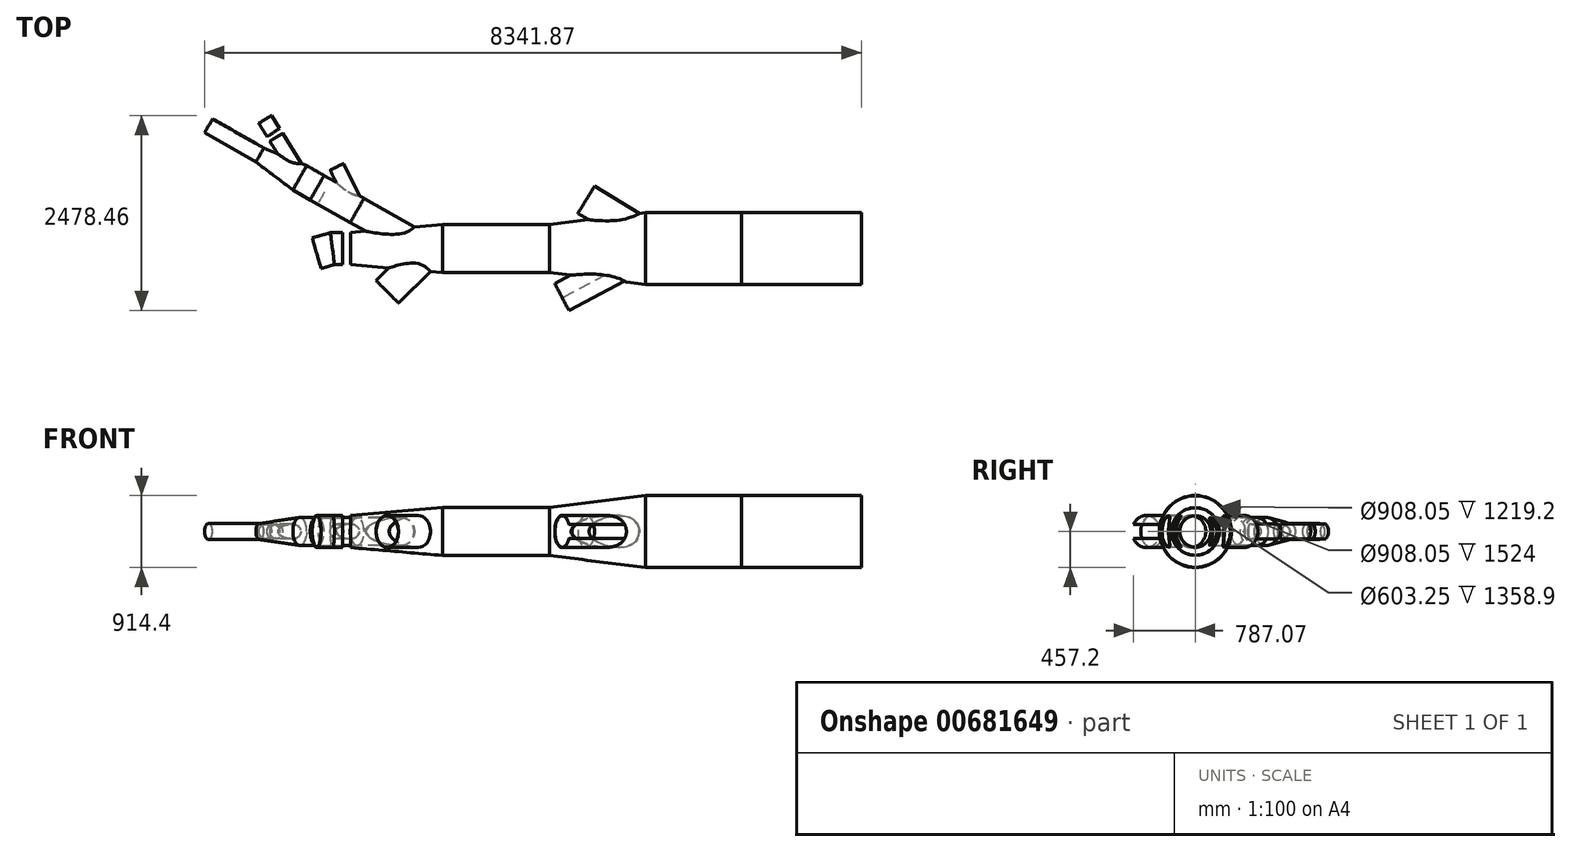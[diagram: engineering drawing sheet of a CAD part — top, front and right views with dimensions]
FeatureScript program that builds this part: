
annotation { "Feature Type Name" : "Feature", "Feature Type Description" : "" }
export const myFeature = defineFeature(function(context is Context, id is Id, definition is map)
    precondition{}
    {
        {
            var Q0;
            Q0=qCreatedBy(makeId("Top.planeOp"),FACE);
            var sketch = newSketch(context, id + "F0", { "sketchPlane" : qUnion([Q0])});
            skLineSegment(sketch, "E0", {"start": v(0, 0) * mm, "end": v(1524, 0) * mm, "construction": true});
            skLineSegment(sketch, "E1", {"start": v(0, 0) * mm, "end": v(-1219.2, 0) * mm, "construction": true});
            skLineSegment(sketch, "E2", {"start": v(-1219.2, 0) * mm, "end": v(-2438.4, 0) * mm, "construction": true});
            skLineSegment(sketch, "E3", {"start": v(-2438.4, 0) * mm, "end": v(-3797.3, 0) * mm, "construction": true});
            skLineSegment(sketch, "E4", {"start": v(-3797.3, 0) * mm, "end": v(-4965.7, 0) * mm, "construction": true});
            skLineSegment(sketch, "E5", {"start": v(-4965.7, 0) * mm, "end": v(-5067.3, 0) * mm, "construction": true});
            skLineSegment(sketch, "E6", {"start": v(1524, 0) * mm, "end": v(1524, 457.2) * mm, "construction": true});
            skLineSegment(sketch, "E7", {"start": v(1524, 0) * mm, "end": v(1524, -457.2) * mm, "construction": true});
            skLineSegment(sketch, "E8", {"start": v(0, 0) * mm, "end": v(0, 457.2) * mm, "construction": true});
            skLineSegment(sketch, "E9", {"start": v(0, 0) * mm, "end": v(0, -457.2) * mm, "construction": true});
            skLineSegment(sketch, "E10", {"start": v(-1219.2, 0) * mm, "end": v(-1219.2, 457.2) * mm, "construction": true});
            skLineSegment(sketch, "E11", {"start": v(-1219.2, 0) * mm, "end": v(-1219.2, -457.2) * mm, "construction": true});
            skLineSegment(sketch, "E12", {"start": v(-2438.4, 0) * mm, "end": v(-2438.4, 304.8) * mm, "construction": true});
            skLineSegment(sketch, "E13", {"start": v(-2438.4, 0) * mm, "end": v(-2438.4, -304.8) * mm, "construction": true});
            skLineSegment(sketch, "E14", {"start": v(-3797.3, 0) * mm, "end": v(-3797.3, 304.8) * mm, "construction": true});
            skLineSegment(sketch, "E15", {"start": v(-3797.3, 0) * mm, "end": v(-3797.3, -304.8) * mm, "construction": true});
            skLineSegment(sketch, "E16", {"start": v(-4965.7, 0) * mm, "end": v(-4965.7, 203.2) * mm, "construction": true});
            skLineSegment(sketch, "E17", {"start": v(-4965.7, 0) * mm, "end": v(-4965.7, -203.2) * mm, "construction": true});
            skLineSegment(sketch, "E18", {"start": v(-5067.3, 0) * mm, "end": v(-5067.3, 203.2) * mm, "construction": true});
            skLineSegment(sketch, "E19", {"start": v(-5067.3, 0) * mm, "end": v(-5067.3, -203.2) * mm, "construction": true});
            skLineSegment(sketch, "E20", {"start": v(-5067.3, 203.2) * mm, "end": v(-5219.7, 203.2) * mm, "construction": true});
            skLineSegment(sketch, "E21", {"start": v(-5067.3, -203.2) * mm, "end": v(-5168.9, -203.2) * mm, "construction": true});
            skLineSegment(sketch, "E22", {"start": v(-5168.9, -203.2) * mm, "end": v(-5219.7, 203.2) * mm, "construction": true});
            skLineSegment(sketch, "E23", {"start": v(-5219.7, 203.2) * mm, "end": v(-5451.6, 136.5) * mm, "construction": true});
            skLineSegment(sketch, "E24", {"start": v(-5451.6, 136.5) * mm, "end": v(-5339.27, -254.06) * mm, "construction": true});
            skLineSegment(sketch, "E25", {"start": v(-5339.27, -254.06) * mm, "end": v(-5168.9, -203.2) * mm, "construction": true});
            skLineSegment(sketch, "E26", {"start": v(-4965.7, -203.2) * mm, "end": v(-3797.3, -304.8) * mm, "construction": true});
            skLineSegment(sketch, "E27", {"start": v(-1219.2, 457.2) * mm, "end": v(0, 457.2) * mm, "construction": true});
            skLineSegment(sketch, "E28", {"start": v(1524, 457.2) * mm, "end": v(0, 457.2) * mm, "construction": true});
            skLineSegment(sketch, "E29", {"start": v(-1219.2, -457.2) * mm, "end": v(0, -457.2) * mm, "construction": true});
            skLineSegment(sketch, "E30", {"start": v(1524, -457.2) * mm, "end": v(0, -457.2) * mm, "construction": true});
            skLineSegment(sketch, "E31", {"start": v(-3797.3, 304.8) * mm, "end": v(-2438.4, 304.8) * mm, "construction": true});
            skLineSegment(sketch, "E32", {"start": v(-3797.3, -304.8) * mm, "end": v(-2438.4, -304.8) * mm, "construction": true});
            skLineSegment(sketch, "E33", {"start": v(-5067.3, 203.2) * mm, "end": v(-4965.7, 203.2) * mm, "construction": true});
            skLineSegment(sketch, "E34", {"start": v(-5067.3, -203.2) * mm, "end": v(-4965.7, -203.2) * mm, "construction": true});
            skLineSegment(sketch, "E35", {"start": v(-2438.4, 304.8) * mm, "end": v(-1946.92, 366.23) * mm, "construction": true});
            skLineSegment(sketch, "E36", {"start": v(-1946.92, 366.23) * mm, "end": v(-2077.03, 445.6) * mm});
            skLineSegment(sketch, "E37", {"start": v(-2077.03, 445.6) * mm, "end": v(-1865.38, 792.54) * mm});
            skLineSegment(sketch, "E38", {"start": v(-1865.38, 792.54) * mm, "end": v(-1301.6, 448.62) * mm});
            skLineSegment(sketch, "E39", {"start": v(-2438.4, -304.8) * mm, "end": v(-2167.46, -338.67) * mm, "construction": true});
            skLineSegment(sketch, "E40", {"start": v(-2167.46, -338.67) * mm, "end": v(-2369.86, -444.93) * mm});
            skLineSegment(sketch, "E41", {"start": v(-2369.86, -444.93) * mm, "end": v(-2180.95, -804.75) * mm});
            skLineSegment(sketch, "E42", {"start": v(-2180.95, -804.75) * mm, "end": v(-1461.3, -426.94) * mm});
            skLineSegment(sketch, "E43", {"start": v(-2167.46, -338.67) * mm, "end": v(-1219.2, -457.2) * mm, "construction": true});
            skLineSegment(sketch, "E44", {"start": v(-1946.92, 366.23) * mm, "end": v(-1219.2, 457.2) * mm, "construction": true});
            skLineSegment(sketch, "E45", {"start": v(-4965.7, 203.2) * mm, "end": v(-4775.92, 219.7) * mm, "construction": true});
            skLineSegment(sketch, "E46", {"start": v(-4775.92, 219.7) * mm, "end": v(-4969, 329.78) * mm});
            skLineSegment(sketch, "E47", {"start": v(-4969, 329.78) * mm, "end": v(-4792.87, 638.7) * mm, "construction": true});
            skLineSegment(sketch, "E48", {"start": v(-4792.87, 638.7) * mm, "end": v(-4152.96, 273.87) * mm});
            skLineSegment(sketch, "E49", {"start": v(-4775.92, 219.7) * mm, "end": v(-3797.3, 304.8) * mm, "construction": true});
            skLineSegment(sketch, "E50", {"start": v(-4965.7, -203.2) * mm, "end": v(-4478.59, -245.56) * mm, "construction": true});
            skLineSegment(sketch, "E51", {"start": v(-4478.59, -245.56) * mm, "end": v(-4640.5, -406.93) * mm});
            skLineSegment(sketch, "E52", {"start": v(-4640.5, -406.93) * mm, "end": v(-4353.62, -694.78) * mm});
            skLineSegment(sketch, "E53", {"start": v(-4353.62, -694.78) * mm, "end": v(-3948.83, -291.35) * mm});
            skLineSegment(sketch, "E54", {"start": v(-1971.2, 619.07) * mm, "end": v(-1623.1, 406.71) * mm, "construction": true});
            skLineSegment(sketch, "E55", {"start": v(-4497.06, -550.86) * mm, "end": v(-4213.84, -268.58) * mm, "construction": true});
            skLineSegment(sketch, "E56", {"start": v(-4880.93, 484.24) * mm, "end": v(-4464.44, 246.79) * mm, "construction": true});
            skLineSegment(sketch, "E57", {"start": v(-2275.4, -624.84) * mm, "end": v(-1814.38, -382.8) * mm, "construction": true});
            skLineSegment(sketch, "E58", {"start": v(-5395.43, -58.78) * mm, "end": v(-5194.19, -0.9) * mm, "construction": true});
            skLineSegment(sketch, "E59", {"start": v(-5067.3, 0) * mm, "end": v(-5194.19, -0.9) * mm, "construction": true});
            skLineSegment(sketch, "E60", {"start": v(-4880.93, 484.24) * mm, "end": v(-5388.44, 773.59) * mm, "construction": true});
            skLineSegment(sketch, "E61", {"start": v(-5388.44, 773.59) * mm, "end": v(-5609.1, 899.39) * mm, "construction": true});
            skLineSegment(sketch, "E62", {"start": v(-5609.1, 899.39) * mm, "end": v(-6116.61, 1188.74) * mm, "construction": true});
            skLineSegment(sketch, "E63", {"start": v(-6116.61, 1188.74) * mm, "end": v(-6767.55, 1559.85) * mm, "construction": true});
            skLineSegment(sketch, "E64", {"start": v(-6767.55, 1559.85) * mm, "end": v(-6717.23, 1648.12) * mm, "construction": true});
            skLineSegment(sketch, "E65", {"start": v(-6767.55, 1559.85) * mm, "end": v(-6817.87, 1471.6) * mm, "construction": true});
            skLineSegment(sketch, "E66", {"start": v(-5388.44, 773.59) * mm, "end": v(-5300.38, 928.05) * mm, "construction": true});
            skLineSegment(sketch, "E67", {"start": v(-5609.1, 899.39) * mm, "end": v(-5521.04, 1053.85) * mm, "construction": true});
            skLineSegment(sketch, "E68", {"start": v(-6116.61, 1188.74) * mm, "end": v(-6066.29, 1277) * mm, "construction": true});
            skLineSegment(sketch, "E69", {"start": v(-5388.44, 773.59) * mm, "end": v(-5476.5, 619.13) * mm, "construction": true});
            skLineSegment(sketch, "E70", {"start": v(-5609.1, 899.39) * mm, "end": v(-5697.16, 744.93) * mm, "construction": true});
            skLineSegment(sketch, "E71", {"start": v(-6116.61, 1188.74) * mm, "end": v(-6166.93, 1100.47) * mm, "construction": true});
            skLineSegment(sketch, "E72", {"start": v(-6066.29, 1277) * mm, "end": v(-5521.04, 1053.85) * mm, "construction": true});
            skLineSegment(sketch, "E73", {"start": v(-4792.87, 638.7) * mm, "end": v(-5300.38, 928.05) * mm, "construction": true});
            skLineSegment(sketch, "E74", {"start": v(-5300.38, 928.05) * mm, "end": v(-5156.95, 846.28) * mm});
            skLineSegment(sketch, "E75", {"start": v(-5156.95, 846.28) * mm, "end": v(-5228.95, 994.85) * mm});
            skLineSegment(sketch, "E76", {"start": v(-5228.95, 994.85) * mm, "end": v(-5046.1, 1083.46) * mm});
            skLineSegment(sketch, "E77", {"start": v(-5046.1, 1083.46) * mm, "end": v(-4846.7, 672.03) * mm});
            skLineSegment(sketch, "E78", {"start": v(-6066.29, 1277) * mm, "end": v(-5901.74, 1209.65) * mm});
            skLineSegment(sketch, "E79", {"start": v(-5901.74, 1209.65) * mm, "end": v(-5995.1, 1360.97) * mm});
            skLineSegment(sketch, "E80", {"start": v(-5995.1, 1360.97) * mm, "end": v(-5822.16, 1467.67) * mm});
            skLineSegment(sketch, "E81", {"start": v(-5822.16, 1467.67) * mm, "end": v(-5582.1, 1078.56) * mm});
            skLineSegment(sketch, "E82", {"start": v(-5908.63, 1414.32) * mm, "end": v(-5742.03, 1144.3) * mm, "construction": true});
            skLineSegment(sketch, "E83", {"start": v(-5137.52, 1039.16) * mm, "end": v(-5000.95, 757.33) * mm, "construction": true});
            skLineSegment(sketch, "E84", {"start": v(-5228.95, 994.85) * mm, "end": v(-5259.41, 1057.7) * mm});
            skLineSegment(sketch, "E85", {"start": v(-5259.41, 1057.7) * mm, "end": v(-5076.56, 1146.32) * mm, "construction": true});
            skLineSegment(sketch, "E86", {"start": v(-5076.56, 1146.32) * mm, "end": v(-5046.1, 1083.46) * mm});
            skLineSegment(sketch, "E87", {"start": v(-5995.1, 1360.97) * mm, "end": v(-6031.77, 1420.42) * mm, "construction": true});
            skLineSegment(sketch, "E88", {"start": v(-6031.77, 1420.42) * mm, "end": v(-5858.84, 1527.11) * mm, "construction": true});
            skLineSegment(sketch, "E89", {"start": v(-5858.84, 1527.11) * mm, "end": v(-5822.16, 1467.67) * mm, "construction": true});
            skLineSegment(sketch, "E90", {"start": v(-6031.77, 1420.42) * mm, "end": v(-6135.13, 1587.95) * mm, "construction": true});
            skLineSegment(sketch, "E91", {"start": v(-6135.13, 1587.95) * mm, "end": v(-6048.66, 1641.3) * mm, "construction": true});
            skLineSegment(sketch, "E92", {"start": v(-6048.66, 1641.3) * mm, "end": v(-5908.63, 1414.32) * mm, "construction": true});
            skLineSegment(sketch, "E93", {"start": v(-6048.66, 1641.3) * mm, "end": v(-5962.2, 1694.64) * mm, "construction": true});
            skLineSegment(sketch, "E94", {"start": v(-5962.2, 1694.64) * mm, "end": v(-5858.84, 1527.11) * mm, "construction": true});
            skSolve(sketch);
        }
        {
            var Q0;
            Q0=sQuery(id+"F0.wireOp",EDGE,"E7");
            cPlane(context, id + "F1", {"entities" : qUnion([Q0]), "cplaneType" : CPlaneType.LINE_ANGLE, "offset" : 0 * mm, "angle" : 90 * degree, "width" : 152.4 * mm, "height" : 152.4 * mm});
        }
        {
            var Q0;
            Q0=sQuery(id+"F0.wireOp",EDGE,"E9");
            cPlane(context, id + "F2", {"entities" : qUnion([Q0]), "cplaneType" : CPlaneType.LINE_ANGLE, "offset" : 0 * mm, "angle" : 90 * degree, "width" : 152.4 * mm, "height" : 152.4 * mm});
        }
        {
            var Q0;
            Q0=sQuery(id+"F0.wireOp",EDGE,"E11");
            cPlane(context, id + "F3", {"entities" : qUnion([Q0]), "cplaneType" : CPlaneType.LINE_ANGLE, "offset" : 0 * mm, "angle" : 90 * degree, "width" : 152.4 * mm, "height" : 152.4 * mm});
        }
        {
            var Q0;
            Q0=sQuery(id+"F0.wireOp",EDGE,"E13");
            cPlane(context, id + "F4", {"entities" : qUnion([Q0]), "cplaneType" : CPlaneType.LINE_ANGLE, "offset" : 25.4 * mm, "angle" : 90 * degree, "width" : 152.4 * mm, "height" : 152.4 * mm});
        }
        {
            var Q0;
            Q0=sQuery(id+"F0.wireOp",EDGE,"E15");
            cPlane(context, id + "F5", {"entities" : qUnion([Q0]), "cplaneType" : CPlaneType.LINE_ANGLE, "offset" : 25.4 * mm, "angle" : 90 * degree, "width" : 152.4 * mm, "height" : 152.4 * mm});
        }
        {
            var Q0;
            Q0=sQuery(id+"F0.wireOp",EDGE,"E17");
            cPlane(context, id + "F6", {"entities" : qUnion([Q0]), "cplaneType" : CPlaneType.LINE_ANGLE, "offset" : 25.4 * mm, "angle" : 90 * degree, "width" : 152.4 * mm, "height" : 152.4 * mm});
        }
        {
            var Q0;
            Q0=sQuery(id+"F0.wireOp",EDGE,"E19");
            cPlane(context, id + "F7", {"entities" : qUnion([Q0]), "cplaneType" : CPlaneType.LINE_ANGLE, "offset" : 25.4 * mm, "angle" : 90 * degree, "width" : 152.4 * mm, "height" : 152.4 * mm});
        }
        {
            var Q0;
            Q0=sQuery(id+"F0.wireOp",EDGE,"E22");
            cPlane(context, id + "F8", {"entities" : qUnion([Q0]), "cplaneType" : CPlaneType.LINE_ANGLE, "offset" : 25.4 * mm, "angle" : 90 * degree, "width" : 152.4 * mm, "height" : 152.4 * mm});
        }
        {
            var Q0;
            Q0=sQuery(id+"F0.wireOp",EDGE,"E24");
            cPlane(context, id + "F9", {"entities" : qUnion([Q0]), "cplaneType" : CPlaneType.LINE_ANGLE, "offset" : 25.4 * mm, "angle" : 90 * degree, "width" : 152.4 * mm, "height" : 152.4 * mm});
        }
        {
            var Q0;
            Q0=sQuery(id+"F0.wireOp",EDGE,"E37");
            cPlane(context, id + "F10", {"entities" : qUnion([Q0]), "cplaneType" : CPlaneType.LINE_ANGLE, "offset" : 25.4 * mm, "angle" : 90 * degree, "width" : 152.4 * mm, "height" : 152.4 * mm});
        }
        {
            var Q0;
            Q0=sQuery(id+"F0.wireOp",EDGE,"E41");
            cPlane(context, id + "F11", {"entities" : qUnion([Q0]), "cplaneType" : CPlaneType.LINE_ANGLE, "offset" : 25.4 * mm, "angle" : 90 * degree, "width" : 152.4 * mm, "height" : 152.4 * mm});
        }
        {
            var Q0;
            Q0=sQuery(id+"F0.wireOp",EDGE,"E47");
            cPlane(context, id + "F12", {"entities" : qUnion([Q0]), "cplaneType" : CPlaneType.LINE_ANGLE, "offset" : 25.4 * mm, "angle" : 90 * degree, "width" : 152.4 * mm, "height" : 152.4 * mm});
        }
        {
            var Q0;
            Q0=sQuery(id+"F0.wireOp",EDGE,"E52");
            cPlane(context, id + "F13", {"entities" : qUnion([Q0]), "cplaneType" : CPlaneType.LINE_ANGLE, "offset" : 25.4 * mm, "angle" : 90 * degree, "width" : 152.4 * mm, "height" : 152.4 * mm});
        }
        {
            var Q0;
            Q0=qCreatedBy(id+"F1.planeOp",FACE);
            var sketch = newSketch(context, id + "F14", { "sketchPlane" : qUnion([Q0])});
            skCircle(sketch, "E95", {"center": v(0, 0) * mm, "radius": 457.2 * mm});
            skCircle(sketch, "E96", {"center": v(0, 0) * mm, "radius": 454.03 * mm});
            skSolve(sketch);
        }
        {
            var Q0;
            Q0=makeQuery(id+"F14.imprint","IMPRINT",FACE,{"disambiguationData":[TD([[makeQuery(id+"F14.imprint","IMPRINT",EDGE,{"derivedFrom":sQuery(id+"F14.wireOp",EDGE,"E95")}),1.0]])]});
            extrude(context, id + "F15", {"entities" : qUnion([Q0]), "oppositeDirection" : true, "depth" : 1524 * mm, "offsetDistance" : 25.4 * mm});
        }
        {
            var Q0;
            Q0=qCreatedBy(id+"F2.planeOp",FACE);
            var sketch = newSketch(context, id + "F16", { "sketchPlane" : qUnion([Q0])});
            skCircle(sketch, "E97", {"center": v(0, 0) * mm, "radius": 454.03 * mm});
            skCircle(sketch, "E98", {"center": v(0, 0) * mm, "radius": 457.2 * mm});
            skSolve(sketch);
        }
        {
            var Q0;
            Q0=makeQuery(id+"F16.imprint","IMPRINT",FACE,{"disambiguationData":[TD([[makeQuery(id+"F16.imprint","IMPRINT",EDGE,{"derivedFrom":sQuery(id+"F16.wireOp",EDGE,"E97")}),-1.0]])]});
            extrude(context, id + "F17", {"entities" : qUnion([Q0]), "oppositeDirection" : true, "depth" : 1219.2 * mm, "offsetDistance" : 25.4 * mm});
        }
        {
            var Q0;
            Q0=qCreatedBy(id+"F3.planeOp",FACE);
            var sketch = newSketch(context, id + "F18", { "sketchPlane" : qUnion([Q0])});
            skCircle(sketch, "E99", {"center": v(0, 0) * mm, "radius": 457.2 * mm});
            skSolve(sketch);
        }
        {
            var Q0;
            Q0=qCreatedBy(id+"F4.planeOp",FACE);
            var sketch = newSketch(context, id + "F19", { "sketchPlane" : qUnion([Q0])});
            skCircle(sketch, "E100", {"center": v(0, 0) * mm, "radius": 304.8 * mm});
            skSolve(sketch);
        }
        {
            var Q0;
            Q0=qCreatedBy(id+"F10.planeOp",FACE);
            var sketch = newSketch(context, id + "F20", { "sketchPlane" : qUnion([Q0])});
            skCircle(sketch, "E101", {"center": v(-495.72, 0) * mm, "radius": 203.2 * mm});
            skSolve(sketch);
        }
        {
            var Q0;
            Q0=makeQuery(id+"F20.imprint","IMPRINT",FACE,{"disambiguationData":[TD([[makeQuery(id+"F20.imprint","IMPRINT",EDGE,{"derivedFrom":sQuery(id+"F20.wireOp",EDGE,"E101")}),1.0]])]});
            extrude(context, id + "F21", {"entities" : qUnion([Q0]), "depth" : 716.28 * mm, "offsetDistance" : 25.4 * mm});
        }
        {
            var Q0;
            Q0=qCreatedBy(id+"F11.planeOp",FACE);
            var sketch = newSketch(context, id + "F22", { "sketchPlane" : qUnion([Q0])});
            skCircle(sketch, "E102", {"center": v(504.45, 0) * mm, "radius": 203.2 * mm});
            skSolve(sketch);
        }
        {
            var Q0;
            Q0=makeQuery(id+"F22.imprint","IMPRINT",FACE,{"disambiguationData":[TD([[makeQuery(id+"F22.imprint","IMPRINT",EDGE,{"derivedFrom":sQuery(id+"F22.wireOp",EDGE,"E102")}),1.0]])]});
            extrude(context, id + "F23", {"entities" : qUnion([Q0]), "depth" : 833.12 * mm, "offsetDistance" : 25.4 * mm});
        }
        {
            var Q2;
            Q2=makeQuery(id+"F19.imprint","IMPRINT",FACE,{"disambiguationData":[TD([[makeQuery(id+"F19.imprint","IMPRINT",EDGE,{"derivedFrom":sQuery(id+"F19.wireOp",EDGE,"E100")}),1.0]])]});
            var Q3;
            Q3=makeQuery(id+"F18.imprint","IMPRINT",FACE,{"disambiguationData":[TD([[makeQuery(id+"F18.imprint","IMPRINT",EDGE,{"derivedFrom":sQuery(id+"F18.wireOp",EDGE,"E99")}),1.0]])]});
            loft(context, id + "F24", {"operationType" : NewBodyOperationType.REMOVE, "sheetProfilesArray" : [{ "sheetProfileEntities" : qUnion([Q2]) }, { "sheetProfileEntities" : qUnion([Q3]) }]});
        }
        {
            var Q0;
            Q0=qCreatedBy(id+"F4.planeOp",FACE);
            var sketch = newSketch(context, id + "F25", { "sketchPlane" : qUnion([Q0])});
            skCircle(sketch, "E103", {"center": v(0, 0) * mm, "radius": 304.8 * mm});
            skSolve(sketch);
        }
        {
            var Q0;
            Q0=qCreatedBy(id+"F3.planeOp",FACE);
            var sketch = newSketch(context, id + "F26", { "sketchPlane" : qUnion([Q0])});
            skCircle(sketch, "E104", {"center": v(0, 0) * mm, "radius": 457.2 * mm});
            skSolve(sketch);
        }
        {
            var Q0;
            Q0=makeQuery(id+"F25.imprint","IMPRINT",FACE,{"disambiguationData":[TD([[makeQuery(id+"F25.imprint","IMPRINT",EDGE,{"derivedFrom":sQuery(id+"F25.wireOp",EDGE,"E103")}),1.0]])]});
            var Q1;
            Q1=makeQuery(id+"F26.imprint","IMPRINT",FACE,{"disambiguationData":[TD([[makeQuery(id+"F26.imprint","IMPRINT",EDGE,{"derivedFrom":sQuery(id+"F26.wireOp",EDGE,"E104")}),1.0]])]});
            loft(context, id + "F27", {"sheetProfilesArray" : [{ "sheetProfileEntities" : qUnion([Q0]) }, { "sheetProfileEntities" : qUnion([Q1]) }]});
        }
        {
            var Q0;
            Q0=makeQuery(id+"F27.opLoft","CAP_FACE",FACE,{"disambiguationData":[OSD([makeQuery(id+"F26.imprint","IMPRINT",FACE,{"disambiguationData":[TD([[makeQuery(id+"F26.imprint","IMPRINT",EDGE,{"derivedFrom":sQuery(id+"F26.wireOp",EDGE,"E104")}),1.0]])]})])],"isStart":true});
            var Q1;
            Q1=makeQuery(id+"F27.opLoft","CAP_FACE",FACE,{"disambiguationData":[OSD([makeQuery(id+"F25.imprint","IMPRINT",FACE,{"disambiguationData":[TD([[makeQuery(id+"F25.imprint","IMPRINT",EDGE,{"derivedFrom":sQuery(id+"F25.wireOp",EDGE,"E103")}),1.0]])]})])],"isStart":true});
            shell(context, id + "F28", {"entities" : qUnion([Q0, Q1]), "thickness" : 2.54 * mm});
        }
        {
            var Q0;
            Q0=makeQuery(id+"F24.boolean.opBoolean","COPY",FACE,{"disambiguationData":[TD([makeQuery(id+"F23.opExtrude","SWEPT_FACE",FACE,{"disambiguationData":[OSD([sQuery(id+"F22.wireOp",EDGE,"E102")])]})])],"derivedFrom":makeQuery(id+"F24.opLoft","SWEPT_FACE",FACE,{"disambiguationData":[OSD([sQuery(id+"F18.wireOp",EDGE,"E99"),sQuery(id+"F19.wireOp",EDGE,"E100")])]})});
            var Q1;
            Q1=makeQuery(id+"F23.opExtrude","CAP_FACE",FACE,{"disambiguationData":[OSD([sQuery(id+"F22.wireOp",EDGE,"E102")])],"isStart":true});
            shell(context, id + "F29", {"entities" : qUnion([Q0, Q1]), "thickness" : 3.17 * mm});
        }
        {
            var Q0;
            Q0=makeQuery(id+"F21.opExtrude","CAP_FACE",FACE,{"disambiguationData":[OSD([sQuery(id+"F20.wireOp",EDGE,"E101")])],"isStart":true});
            var Q1;
            Q1=makeQuery(id+"F24.boolean.opBoolean","COPY",FACE,{"disambiguationData":[TD([makeQuery(id+"F21.opExtrude","SWEPT_FACE",FACE,{"disambiguationData":[OSD([sQuery(id+"F20.wireOp",EDGE,"E101")])]})])],"derivedFrom":makeQuery(id+"F24.opLoft","SWEPT_FACE",FACE,{"disambiguationData":[OSD([sQuery(id+"F18.wireOp",EDGE,"E99"),sQuery(id+"F19.wireOp",EDGE,"E100")])]})});
            shell(context, id + "F30", {"entities" : qUnion([Q0, Q1]), "thickness" : 3.17 * mm});
        }
        {
            var Q0;
            Q0=qCreatedBy(id+"F11.planeOp",FACE);
            var sketch = newSketch(context, id + "F31", { "sketchPlane" : qUnion([Q0])});
            skCircle(sketch, "E105", {"center": v(500.93, 0) * mm, "radius": 200.03 * mm});
            skSolve(sketch);
        }
        {
            var Q0;
            Q0=makeQuery(id+"F31.imprint","IMPRINT",FACE,{"disambiguationData":[TD([[makeQuery(id+"F31.imprint","IMPRINT",EDGE,{"derivedFrom":sQuery(id+"F31.wireOp",EDGE,"E105")}),1.0]])]});
            extrude(context, id + "F32", {"entities" : qUnion([Q0]), "operationType" : NewBodyOperationType.REMOVE, "depth" : 967.74 * mm, "offsetDistance" : 25.4 * mm});
        }
        {
            var Q0;
            Q0=qCreatedBy(id+"F10.planeOp",FACE);
            var sketch = newSketch(context, id + "F33", { "sketchPlane" : qUnion([Q0])});
            skCircle(sketch, "E106", {"center": v(-495.83, 0) * mm, "radius": 200.03 * mm});
            skSolve(sketch);
        }
        {
            var Q0;
            Q0 = qSketchRegion(id + "F33", true);
            extrude(context, id + "F34", {"entities" : qUnion([Q0]), "operationType" : NewBodyOperationType.REMOVE, "depth" : 728.98 * mm, "offsetDistance" : 25.4 * mm});
        }
        {
            var Q0;
            Q0=qCreatedBy(id+"F5.planeOp",FACE);
            var sketch = newSketch(context, id + "F35", { "sketchPlane" : qUnion([Q0])});
            skCircle(sketch, "E107", {"center": v(0, 0) * mm, "radius": 304.8 * mm});
            skCircle(sketch, "E108", {"center": v(0, 0) * mm, "radius": 301.63 * mm});
            skSolve(sketch);
        }
        {
            var Q0;
            Q0=makeQuery(id+"F35.imprint","IMPRINT",FACE,{"disambiguationData":[TD([[makeQuery(id+"F35.imprint","IMPRINT",EDGE,{"derivedFrom":sQuery(id+"F35.wireOp",EDGE,"E107")}),1.0]])]});
            extrude(context, id + "F36", {"entities" : qUnion([Q0]), "depth" : 1358.9 * mm, "offsetDistance" : 25.4 * mm});
        }
        {
            var Q0;
            Q0=qCreatedBy(id+"F5.planeOp",FACE);
            var sketch = newSketch(context, id + "F37", { "sketchPlane" : qUnion([Q0])});
            skCircle(sketch, "E109", {"center": v(0, 0) * mm, "radius": 304.8 * mm});
            skSolve(sketch);
        }
        {
            var Q0;
            Q0=qCreatedBy(id+"F13.planeOp",FACE);
            var sketch = newSketch(context, id + "F38", { "sketchPlane" : qUnion([Q0])});
            skCircle(sketch, "E110", {"center": v(2785.05, 0) * mm, "radius": 203.2 * mm});
            skSolve(sketch);
        }
        {
            var Q0;
            Q0=qCreatedBy(id+"F12.planeOp",FACE);
            var sketch = newSketch(context, id + "F39", { "sketchPlane" : qUnion([Q0])});
            skCircle(sketch, "E111", {"center": v(-1996.73, 0) * mm, "radius": 177.8 * mm});
            skSolve(sketch);
        }
        {
            var Q0;
            Q0=qCreatedBy(id+"F6.planeOp",FACE);
            var sketch = newSketch(context, id + "F40", { "sketchPlane" : qUnion([Q0])});
            skCircle(sketch, "E112", {"center": v(0, 0) * mm, "radius": 203.2 * mm});
            skSolve(sketch);
        }
        {
            var Q0;
            Q0=makeQuery(id+"F39.imprint","IMPRINT",FACE,{"disambiguationData":[TD([[makeQuery(id+"F39.imprint","IMPRINT",EDGE,{"derivedFrom":sQuery(id+"F39.wireOp",EDGE,"E111")}),1.0]])]});
            extrude(context, id + "F41", {"entities" : qUnion([Q0]), "depth" : 782.32 * mm, "offsetDistance" : 25.4 * mm});
        }
        {
            var Q0;
            Q0=makeQuery(id+"F38.imprint","IMPRINT",FACE,{"disambiguationData":[TD([[makeQuery(id+"F38.imprint","IMPRINT",EDGE,{"derivedFrom":sQuery(id+"F38.wireOp",EDGE,"E110")}),1.0]])]});
            var Q1;
            Q1=sQuery(id+"F38.wireOp",EDGE,"E110");
            extrude(context, id + "F42", {"entities" : qUnion([Q0]), "operationType" : NewBodyOperationType.ADD, "surfaceEntities" : qUnion([Q1]), "depth" : 599.44 * mm, "offsetDistance" : 25.4 * mm});
        }
        {
            var Q1;
            Q1=makeQuery(id+"F40.imprint","IMPRINT",FACE,{"disambiguationData":[TD([[makeQuery(id+"F40.imprint","IMPRINT",EDGE,{"derivedFrom":sQuery(id+"F40.wireOp",EDGE,"E112")}),1.0]])]});
            var Q2;
            Q2=makeQuery(id+"F37.imprint","IMPRINT",FACE,{"disambiguationData":[TD([[makeQuery(id+"F37.imprint","IMPRINT",EDGE,{"derivedFrom":sQuery(id+"F37.wireOp",EDGE,"E109")}),1.0]])]});
            loft(context, id + "F43", {"operationType" : NewBodyOperationType.REMOVE, "sheetProfilesArray" : [{ "sheetProfileEntities" : qUnion([Q1]) }, { "sheetProfileEntities" : qUnion([Q2]) }]});
        }
        {
            var Q0;
            Q0=qCreatedBy(id+"F12.planeOp",FACE);
            var sketch = newSketch(context, id + "F44", { "sketchPlane" : qUnion([Q0])});
            skCircle(sketch, "E113", {"center": v(-1996.78, 0) * mm, "radius": 174.63 * mm});
            skSolve(sketch);
        }
        {
            var Q0;
            Q0=qCreatedBy(id+"F13.planeOp",FACE);
            var sketch = newSketch(context, id + "F45", { "sketchPlane" : qUnion([Q0])});
            skCircle(sketch, "E114", {"center": v(2784.4, 0) * mm, "radius": 200.03 * mm});
            skSolve(sketch);
        }
        {
            var Q0;
            Q0=makeQuery(id+"F37.imprint","IMPRINT",FACE,{"disambiguationData":[TD([[makeQuery(id+"F37.imprint","IMPRINT",EDGE,{"derivedFrom":sQuery(id+"F37.wireOp",EDGE,"E109")}),1.0]])]});
            var Q1;
            Q1=makeQuery(id+"F40.imprint","IMPRINT",FACE,{"disambiguationData":[TD([[makeQuery(id+"F40.imprint","IMPRINT",EDGE,{"derivedFrom":sQuery(id+"F40.wireOp",EDGE,"E112")}),1.0]])]});
            loft(context, id + "F46", {"sheetProfilesArray" : [{ "sheetProfileEntities" : qUnion([Q0]) }, { "sheetProfileEntities" : qUnion([Q1]) }]});
        }
        {
            var Q0;
            Q0=makeQuery(id+"F46.opLoft","CAP_FACE",FACE,{"disambiguationData":[OSD([makeQuery(id+"F37.imprint","IMPRINT",FACE,{"disambiguationData":[TD([[makeQuery(id+"F37.imprint","IMPRINT",EDGE,{"derivedFrom":sQuery(id+"F37.wireOp",EDGE,"E109")}),1.0]])]})])],"isStart":true});
            var Q1;
            Q1=makeQuery(id+"F46.opLoft","CAP_FACE",FACE,{"disambiguationData":[OSD([makeQuery(id+"F40.imprint","IMPRINT",FACE,{"disambiguationData":[TD([[makeQuery(id+"F40.imprint","IMPRINT",EDGE,{"derivedFrom":sQuery(id+"F40.wireOp",EDGE,"E112")}),1.0]])]})])],"isStart":true});
            shell(context, id + "F47", {"entities" : qUnion([Q0, Q1]), "thickness" : 2.54 * mm});
        }
        {
            var Q0;
            Q0=makeQuery(id+"F45.imprint","IMPRINT",FACE,{"disambiguationData":[TD([[makeQuery(id+"F45.imprint","IMPRINT",EDGE,{"derivedFrom":sQuery(id+"F45.wireOp",EDGE,"E114")}),1.0]])]});
            extrude(context, id + "F48", {"entities" : qUnion([Q0]), "operationType" : NewBodyOperationType.REMOVE, "depth" : 650.24 * mm, "offsetDistance" : 25.4 * mm});
        }
        {
            var Q0;
            Q0=makeQuery(id+"F44.imprint","IMPRINT",FACE,{"disambiguationData":[TD([[makeQuery(id+"F44.imprint","IMPRINT",EDGE,{"derivedFrom":sQuery(id+"F44.wireOp",EDGE,"E113")}),1.0]])]});
            extrude(context, id + "F49", {"entities" : qUnion([Q0]), "operationType" : NewBodyOperationType.REMOVE, "depth" : 853.44 * mm, "offsetDistance" : 25.4 * mm});
        }
        {
            var Q0;
            Q0=makeQuery(id+"F44.imprint","IMPRINT",FACE,{"disambiguationData":[TD([[makeQuery(id+"F44.imprint","IMPRINT",EDGE,{"derivedFrom":sQuery(id+"F44.wireOp",EDGE,"E113")}),1.0]])]});
            extrude(context, id + "F50", {"entities" : qUnion([Q0]), "operationType" : NewBodyOperationType.REMOVE, "depth" : 960.12 * mm, "offsetDistance" : 25.4 * mm});
        }
        {
            var Q0;
            Q0=makeQuery(id+"F45.imprint","IMPRINT",FACE,{"disambiguationData":[TD([[makeQuery(id+"F45.imprint","IMPRINT",EDGE,{"derivedFrom":sQuery(id+"F45.wireOp",EDGE,"E114")}),1.0]])]});
            extrude(context, id + "F51", {"entities" : qUnion([Q0]), "operationType" : NewBodyOperationType.REMOVE, "depth" : 924.56 * mm, "offsetDistance" : 25.4 * mm});
        }
        {
            var Q0;
            Q0=qCreatedBy(id+"F7.planeOp",FACE);
            var sketch = newSketch(context, id + "F52", { "sketchPlane" : qUnion([Q0])});
            skCircle(sketch, "E115", {"center": v(0, 0) * mm, "radius": 203.2 * mm});
            skSolve(sketch);
        }
        {
            var Q0;
            Q0=qCreatedBy(id+"F8.planeOp",FACE);
            var sketch = newSketch(context, id + "F53", { "sketchPlane" : qUnion([Q0])});
            skCircle(sketch, "E116", {"center": v(643.35, 0) * mm, "radius": 203.2 * mm});
            skSolve(sketch);
        }
        {
            var Q0;
            Q0=qCreatedBy(id+"F9.planeOp",FACE);
            var sketch = newSketch(context, id + "F54", { "sketchPlane" : qUnion([Q0])});
            skCircle(sketch, "E117", {"center": v(1434.82, 0) * mm, "radius": 203.2 * mm});
            skSolve(sketch);
        }
        {
            var Q0;
            Q0=makeQuery(id+"F54.imprint","IMPRINT",FACE,{"disambiguationData":[TD([[makeQuery(id+"F54.imprint","IMPRINT",EDGE,{"derivedFrom":sQuery(id+"F54.wireOp",EDGE,"E117")}),1.0]])]});
            var Q1;
            Q1=makeQuery(id+"F53.imprint","IMPRINT",FACE,{"disambiguationData":[TD([[makeQuery(id+"F53.imprint","IMPRINT",EDGE,{"derivedFrom":sQuery(id+"F53.wireOp",EDGE,"E116")}),1.0]])]});
            loft(context, id + "F55", {"sheetProfilesArray" : [{ "sheetProfileEntities" : qUnion([Q0]) }, { "sheetProfileEntities" : qUnion([Q1]) }]});
        }
        {
            var Q1;
            Q1=makeQuery(id+"F52.imprint","IMPRINT",FACE,{"disambiguationData":[TD([[makeQuery(id+"F52.imprint","IMPRINT",EDGE,{"derivedFrom":sQuery(id+"F52.wireOp",EDGE,"E115")}),1.0]])]});
            var Q2;
            Q2=makeQuery(id+"F55.opLoft","CAP_FACE",FACE,{"disambiguationData":[OSD([makeQuery(id+"F53.imprint","IMPRINT",FACE,{"disambiguationData":[TD([[makeQuery(id+"F53.imprint","IMPRINT",EDGE,{"derivedFrom":sQuery(id+"F53.wireOp",EDGE,"E116")}),1.0]])]})])],"isStart":true});
            loft(context, id + "F56", {"operationType" : NewBodyOperationType.ADD, "sheetProfilesArray" : [{ "sheetProfileEntities" : qUnion([Q1]) }, { "sheetProfileEntities" : qUnion([Q2]) }]});
        }
        {
            var Q0;
            Q0=makeQuery(id+"F56.opLoft","CAP_FACE",FACE,{"disambiguationData":[OSD([makeQuery(id+"F52.imprint","IMPRINT",FACE,{"disambiguationData":[TD([[makeQuery(id+"F52.imprint","IMPRINT",EDGE,{"derivedFrom":sQuery(id+"F52.wireOp",EDGE,"E115")}),1.0]])]})])],"isStart":true});
            var Q1;
            Q1=makeQuery(id+"F55.opLoft","CAP_FACE",FACE,{"disambiguationData":[OSD([makeQuery(id+"F54.imprint","IMPRINT",FACE,{"disambiguationData":[TD([[makeQuery(id+"F54.imprint","IMPRINT",EDGE,{"derivedFrom":sQuery(id+"F54.wireOp",EDGE,"E117")}),1.0]])]})])],"isStart":true});
            shell(context, id + "F57", {"entities" : qUnion([Q0, Q1]), "thickness" : 2.54 * mm});
        }
        {
            var Q0;
            Q0=sQuery(id+"F0.wireOp",EDGE,"E69");
            cPlane(context, id + "F58", {"entities" : qUnion([Q0]), "cplaneType" : CPlaneType.LINE_ANGLE, "offset" : 25.4 * mm, "angle" : 90 * degree, "width" : 152.4 * mm, "height" : 152.4 * mm});
        }
        {
            var Q0;
            Q0=sQuery(id+"F0.wireOp",EDGE,"E70");
            cPlane(context, id + "F59", {"entities" : qUnion([Q0]), "cplaneType" : CPlaneType.LINE_ANGLE, "offset" : 25.4 * mm, "angle" : 90 * degree, "width" : 152.4 * mm, "height" : 152.4 * mm});
        }
        {
            var Q0;
            Q0=sQuery(id+"F0.wireOp",EDGE,"E71");
            cPlane(context, id + "F60", {"entities" : qUnion([Q0]), "cplaneType" : CPlaneType.LINE_ANGLE, "offset" : 25.4 * mm, "angle" : 90 * degree, "width" : 152.4 * mm, "height" : 152.4 * mm});
        }
        {
            var Q0;
            Q0=sQuery(id+"F0.wireOp",EDGE,"E93");
            cPlane(context, id + "F61", {"entities" : qUnion([Q0]), "cplaneType" : CPlaneType.LINE_ANGLE, "offset" : 25.4 * mm, "angle" : 0 * degree, "width" : 152.4 * mm, "height" : 152.4 * mm});
        }
        {
            var Q0;
            Q0=sQuery(id+"F0.wireOp",EDGE,"E80");
            cPlane(context, id + "F62", {"entities" : qUnion([Q0]), "cplaneType" : CPlaneType.LINE_ANGLE, "offset" : 25.4 * mm, "angle" : 0 * degree, "width" : 152.4 * mm, "height" : 152.4 * mm});
        }
        {
            var Q0;
            Q0=qCreatedBy(id+"F12.planeOp",FACE);
            var sketch = newSketch(context, id + "F63", { "sketchPlane" : qUnion([Q0])});
            skCircle(sketch, "E118", {"center": v(-1996.65, 0) * mm, "radius": 177.8 * mm});
            skCircle(sketch, "E119", {"center": v(-1996.65, 0) * mm, "radius": 174.63 * mm});
            skSolve(sketch);
        }
        {
            var Q0;
            Q0=makeQuery(id+"F63.imprint","IMPRINT",FACE,{"disambiguationData":[TD([[makeQuery(id+"F63.imprint","IMPRINT",EDGE,{"derivedFrom":sQuery(id+"F63.wireOp",EDGE,"E118")}),1.0]])]});
            extrude(context, id + "F64", {"entities" : qUnion([Q0]), "oppositeDirection" : true, "depth" : 584.2 * mm, "offsetDistance" : 25.4 * mm});
        }
        {
            var Q0;
            Q0=qCreatedBy(id+"F58.planeOp",FACE);
            var sketch = newSketch(context, id + "F65", { "sketchPlane" : qUnion([Q0])});
            skCircle(sketch, "E120", {"center": v(-1996.7, 0) * mm, "radius": 177.8 * mm});
            skCircle(sketch, "E121", {"center": v(-1996.7, 0) * mm, "radius": 174.63 * mm});
            skSolve(sketch);
        }
        {
            var Q0;
            Q0=makeQuery(id+"F65.imprint","IMPRINT",FACE,{"disambiguationData":[TD([[makeQuery(id+"F65.imprint","IMPRINT",EDGE,{"derivedFrom":sQuery(id+"F65.wireOp",EDGE,"E120")}),1.0]])]});
            extrude(context, id + "F66", {"entities" : qUnion([Q0]), "oppositeDirection" : true, "depth" : 254 * mm, "offsetDistance" : 25.4 * mm});
        }
        {
            var Q0;
            Q0=sQuery(id+"F0.wireOp",EDGE,"E76");
            cPlane(context, id + "F67", {"entities" : qUnion([Q0]), "cplaneType" : CPlaneType.LINE_ANGLE, "offset" : 25.4 * mm, "angle" : 0 * degree, "width" : 152.4 * mm, "height" : 152.4 * mm});
        }
        {
            var Q0;
            Q0=qCreatedBy(id+"F67.planeOp",FACE);
            var sketch = newSketch(context, id + "F68", { "sketchPlane" : qUnion([Q0])});
            skCircle(sketch, "E122", {"center": v(4170.22, 0) * mm, "radius": 95.25 * mm});
            skSolve(sketch);
        }
        {
            var Q0;
            Q0=makeQuery(id+"F68.imprint","IMPRINT",FACE,{"disambiguationData":[TD([[makeQuery(id+"F68.imprint","IMPRINT",EDGE,{"derivedFrom":sQuery(id+"F68.wireOp",EDGE,"E122")}),1.0]])]});
            extrude(context, id + "F69", {"entities" : qUnion([Q0]), "operationType" : NewBodyOperationType.REMOVE, "oppositeDirection" : true, "depth" : 474.98 * mm, "offsetDistance" : 25.4 * mm});
        }
        {
            var Q0;
            Q0=qCreatedBy(id+"F67.planeOp",FACE);
            var sketch = newSketch(context, id + "F70", { "sketchPlane" : qUnion([Q0])});
            skCircle(sketch, "E123", {"center": v(4169.88, 0) * mm, "radius": 95.25 * mm});
            skCircle(sketch, "E124", {"center": v(4169.88, 0) * mm, "radius": 92.08 * mm});
            skSolve(sketch);
        }
        {
            var Q0;
            Q0=makeQuery(id+"F70.imprint","IMPRINT",FACE,{"disambiguationData":[TD([[makeQuery(id+"F70.imprint","IMPRINT",EDGE,{"derivedFrom":sQuery(id+"F70.wireOp",EDGE,"E123")}),1.0]])]});
            extrude(context, id + "F71", {"entities" : qUnion([Q0]), "oppositeDirection" : true, "depth" : 495.3 * mm, "offsetDistance" : 25.4 * mm});
        }
        {
            var Q0;
            Q0=makeQuery(id+"F44.imprint","IMPRINT",FACE,{"disambiguationData":[TD([[makeQuery(id+"F44.imprint","IMPRINT",EDGE,{"derivedFrom":sQuery(id+"F44.wireOp",EDGE,"E113")}),1.0]])]});
            extrude(context, id + "F72", {"entities" : qUnion([Q0]), "operationType" : NewBodyOperationType.REMOVE, "oppositeDirection" : true, "depth" : 474.98 * mm, "offsetDistance" : 25.4 * mm});
        }
        {
            var Q0;
            Q0=qCreatedBy(id+"F59.planeOp",FACE);
            var sketch = newSketch(context, id + "F73", { "sketchPlane" : qUnion([Q0])});
            skCircle(sketch, "E125", {"center": v(-1996.43, 0) * mm, "radius": 177.8 * mm});
            skSolve(sketch);
        }
        {
            var Q0;
            Q0=qCreatedBy(id+"F60.planeOp",FACE);
            var sketch = newSketch(context, id + "F74", { "sketchPlane" : qUnion([Q0])});
            skCircle(sketch, "E126", {"center": v(-1996.79, 0) * mm, "radius": 101.6 * mm});
            skSolve(sketch);
        }
        {
            var Q0;
            Q0=qCreatedBy(id+"F62.planeOp",FACE);
            var sketch = newSketch(context, id + "F75", { "sketchPlane" : qUnion([Q0])});
            skCircle(sketch, "E127", {"center": v(4285.72, 0) * mm, "radius": 95.25 * mm});
            skCircle(sketch, "E128", {"center": v(4285.72, 0) * mm, "radius": 92.08 * mm});
            skSolve(sketch);
        }
        {
            var Q0;
            Q0=makeQuery(id+"F75.imprint","IMPRINT",FACE,{"disambiguationData":[TD([[makeQuery(id+"F75.imprint","IMPRINT",EDGE,{"derivedFrom":sQuery(id+"F75.wireOp",EDGE,"E127")}),1.0]])]});
            extrude(context, id + "F76", {"entities" : qUnion([Q0]), "oppositeDirection" : true, "depth" : 482.6 * mm, "offsetDistance" : 25.4 * mm});
        }
        {
            var Q1;
            Q1=makeQuery(id+"F73.imprint","IMPRINT",FACE,{"disambiguationData":[TD([[makeQuery(id+"F73.imprint","IMPRINT",EDGE,{"derivedFrom":sQuery(id+"F73.wireOp",EDGE,"E125")}),1.0]])]});
            var Q2;
            Q2=makeQuery(id+"F74.imprint","IMPRINT",FACE,{"disambiguationData":[TD([[makeQuery(id+"F74.imprint","IMPRINT",EDGE,{"derivedFrom":sQuery(id+"F74.wireOp",EDGE,"E126")}),1.0]])]});
            loft(context, id + "F77", {"operationType" : NewBodyOperationType.REMOVE, "sheetProfilesArray" : [{ "sheetProfileEntities" : qUnion([Q1]) }, { "sheetProfileEntities" : qUnion([Q2]) }]});
        }
        {
            var Q1;
            Q1=makeQuery(id+"F73.imprint","IMPRINT",FACE,{"disambiguationData":[TD([[makeQuery(id+"F73.imprint","IMPRINT",EDGE,{"derivedFrom":sQuery(id+"F73.wireOp",EDGE,"E125")}),1.0]])]});
            var Q2;
            Q2=makeQuery(id+"F74.imprint","IMPRINT",FACE,{"disambiguationData":[TD([[makeQuery(id+"F74.imprint","IMPRINT",EDGE,{"derivedFrom":sQuery(id+"F74.wireOp",EDGE,"E126")}),1.0]])]});
            loft(context, id + "F78", {"sheetProfilesArray" : [{ "sheetProfileEntities" : qUnion([Q1]) }, { "sheetProfileEntities" : qUnion([Q2]) }]});
        }
        {
            var Q0;
            Q0=makeQuery(id+"F78.opLoft","CAP_FACE",FACE,{"disambiguationData":[OSD([makeQuery(id+"F73.imprint","IMPRINT",FACE,{"disambiguationData":[TD([[makeQuery(id+"F73.imprint","IMPRINT",EDGE,{"derivedFrom":sQuery(id+"F73.wireOp",EDGE,"E125")}),1.0]])]})])],"isStart":true});
            var Q1;
            Q1=makeQuery(id+"F78.opLoft","CAP_FACE",FACE,{"disambiguationData":[OSD([makeQuery(id+"F74.imprint","IMPRINT",FACE,{"disambiguationData":[TD([[makeQuery(id+"F74.imprint","IMPRINT",EDGE,{"derivedFrom":sQuery(id+"F74.wireOp",EDGE,"E126")}),1.0]])]})])],"isStart":true});
            shell(context, id + "F79", {"entities" : qUnion([Q0, Q1]), "thickness" : 3.17 * mm});
        }
        {
            var Q0;
            Q0=makeQuery(id+"F75.imprint","IMPRINT",FACE,{"disambiguationData":[TD([[makeQuery(id+"F75.imprint","IMPRINT",EDGE,{"derivedFrom":sQuery(id+"F75.wireOp",EDGE,"E128")}),1.0]])]});
            extrude(context, id + "F80", {"entities" : qUnion([Q0]), "operationType" : NewBodyOperationType.REMOVE, "oppositeDirection" : true, "depth" : 473.7 * mm, "offsetDistance" : 25.4 * mm});
        }
        {
            var Q0;
            Q0=qCreatedBy(id+"F60.planeOp",FACE);
            var sketch = newSketch(context, id + "F81", { "sketchPlane" : qUnion([Q0])});
            skCircle(sketch, "E129", {"center": v(-1996.79, 0) * mm, "radius": 101.6 * mm});
            skCircle(sketch, "E130", {"center": v(-1996.79, 0) * mm, "radius": 98.43 * mm});
            skSolve(sketch);
        }
        {
            var Q0;
            Q0=makeQuery(id+"F81.imprint","IMPRINT",FACE,{"disambiguationData":[TD([[makeQuery(id+"F81.imprint","IMPRINT",EDGE,{"derivedFrom":sQuery(id+"F81.wireOp",EDGE,"E129")}),1.0]])]});
            extrude(context, id + "F82", {"entities" : qUnion([Q0]), "oppositeDirection" : true, "depth" : 749.3 * mm, "offsetDistance" : 25.4 * mm});
        }
        {
            var Q0;
            Q0=qCreatedBy(id+"F61.planeOp",FACE);
            var sketch = newSketch(context, id + "F83", { "sketchPlane" : qUnion([Q0])});
            skCircle(sketch, "E131", {"center": v(4285.82, 0) * mm, "radius": 95.25 * mm});
            skCircle(sketch, "E132", {"center": v(4285.82, 0) * mm, "radius": 92.08 * mm});
            skSolve(sketch);
        }
        {
            var Q0;
            Q0=makeQuery(id+"F83.imprint","IMPRINT",FACE,{"disambiguationData":[TD([[makeQuery(id+"F83.imprint","IMPRINT",EDGE,{"derivedFrom":sQuery(id+"F83.wireOp",EDGE,"E131")}),1.0]])]});
            extrude(context, id + "F84", {"entities" : qUnion([Q0]), "oppositeDirection" : true, "depth" : 196.85 * mm, "offsetDistance" : 25.4 * mm});
        }
    });
